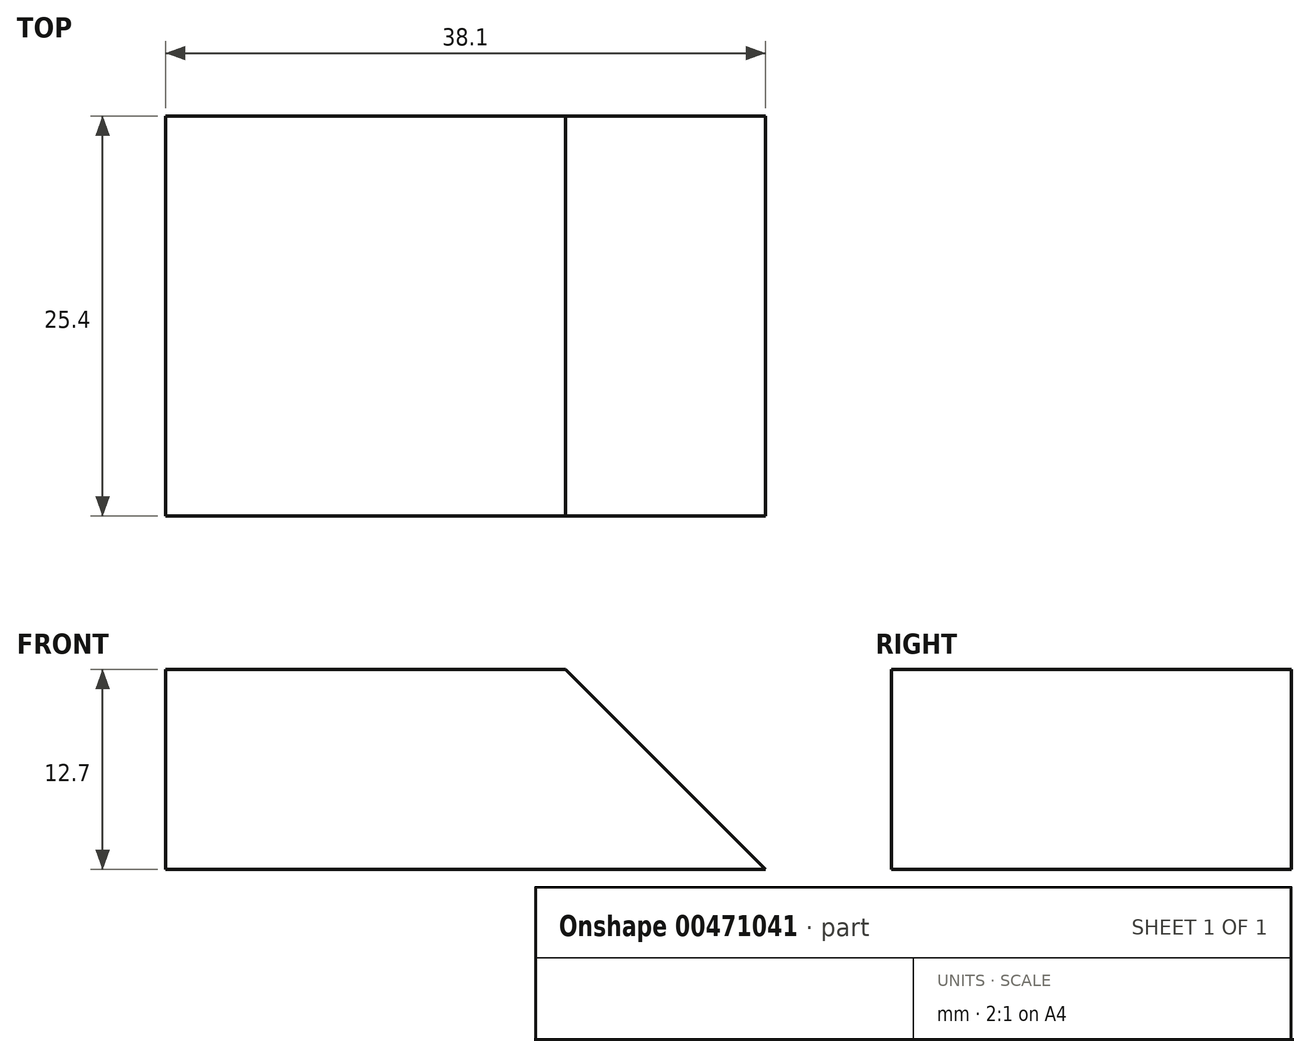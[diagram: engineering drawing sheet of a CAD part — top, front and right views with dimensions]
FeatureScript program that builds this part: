
annotation { "Feature Type Name" : "Feature", "Feature Type Description" : "" }
export const myFeature = defineFeature(function(context is Context, id is Id, definition is map)
    precondition{}
    {
        {
            var Q0;
            Q0=qCreatedBy(makeId("Front.planeOp"),FACE);
            var sketch = newSketch(context, id + "F0", { "sketchPlane" : qUnion([Q0])});
            skLineSegment(sketch, "E0", {"start": v(0, 0) * mm, "end": v(-25.4, 0) * mm});
            skLineSegment(sketch, "E1", {"start": v(-25.4, 0) * mm, "end": v(-25.4, 12.7) * mm});
            skLineSegment(sketch, "E2", {"start": v(-25.4, 12.7) * mm, "end": v(0, 12.7) * mm});
            skLineSegment(sketch, "E3", {"start": v(0, 12.7) * mm, "end": v(12.7, 0) * mm});
            skLineSegment(sketch, "E4", {"start": v(12.7, 0) * mm, "end": v(0, 0) * mm});
            skSolve(sketch);
        }
        {
            var Q0;
            Q0=makeQuery(id+"F0.imprint","IMPRINT",FACE,{"disambiguationData":[TD([[makeQuery(id+"F0.imprint","IMPRINT",EDGE,{"derivedFrom":sQuery(id+"F0.wireOp",EDGE,"E0")}),-1.0]])]});
            extrude(context, id + "F1", {"entities" : qUnion([Q0]), "depth" : 25.4 * mm});
        }
    });
